FCSTD DOCUMENT  (FreeCAD 0.17R13541 (Git))
Label: holder
License: All rights reserved
LicenseURL: http://it.wikipedia.org/wiki/<copyright redacted>
objects: Sketcher::SketchObject×1
note: 1 computed .brp shape members not serialized (recipe doc carries the construction recipe); baked Part::Feature solids carry a one-line shape summary decoded from their .brp

FEATURE [Sketcher::SketchObject] Sketch015
  sketch-geometry (11):
    g0: Circle CenterX=852.386 CenterY=859.444 CenterZ=0 NormalX=0 NormalY=0 NormalZ=-1 AngleXU=0 Radius=1.5
    g1: ArcOfCircle [constr] CenterX=821.884 CenterY=859.444 CenterZ=0 NormalX=0 NormalY=0 NormalZ=1 AngleXU=0 Radius=3.98663 StartAngle=3.14024 EndAngle=5.83885
    g2: Circle CenterX=821.886 CenterY=859.452 CenterZ=0 NormalX=0 NormalY=0 NormalZ=-1 AngleXU=0 Radius=1.5
    g3: ArcOfCircle [constr] CenterX=852.386 CenterY=859.452 CenterZ=0 NormalX=0 NormalY=0 NormalZ=1 AngleXU=0 Radius=4 StartAngle=3.5845 EndAngle=6.28319
    g4: LineSegment [constr] StartX=821.884 StartY=859.444 StartZ=0 EndX=852.386 EndY=859.444 EndZ=0
    g5: GeomPoint X=837.136 Y=859.444 Z=0
    g6: LineSegment [constr] StartX=837.136 StartY=845.083 StartZ=0 EndX=837.136 EndY=864.076 EndZ=0
    g7: ArcOfCircle CenterX=821.884 CenterY=859.444 CenterZ=0 NormalX=0 NormalY=0 NormalZ=1 AngleXU=0 Radius=3.98663 StartAngle=1.58665 EndAngle=3.37787
    g8: ArcOfCircle CenterX=852.388 CenterY=859.435 CenterZ=0 NormalX=0 NormalY=0 NormalZ=1 AngleXU=0 Radius=3.99578 StartAngle=6.02246 EndAngle=7.84479
    g9: LineSegment StartX=821.821 StartY=863.43 StartZ=0 EndX=852.425 EndY=863.43 EndZ=0
    g10: LineSegment StartX=818.008 StartY=858.511 StartZ=0 EndX=820.531 EndY=832.6 EndZ=0
  constraints (16):
    c: Coincident(g4,g1)
    c: Coincident(g0,g4)
    c: PointOnObject(g5,g4)
    c: DistanceX(g0,g-1) = -852.386
    c: DistanceY(g0,g-1) = -859.444
    c: DistanceX(g1,g-1) = -821.884
    c: DistanceY(g1,g-1) = -859.444
    c: Distance(g0,g5) = 15.25
    c: Vertical(g6)
    c: PointOnObject(g5,g6)
    c: Coincident(g7,g1)
    c: PointOnObject(g7,g1)
    c: Coincident(g9,g7)
    c: Coincident(g9,g8)
    c: Horizontal(g9)
    c: Coincident(g10,g7)
